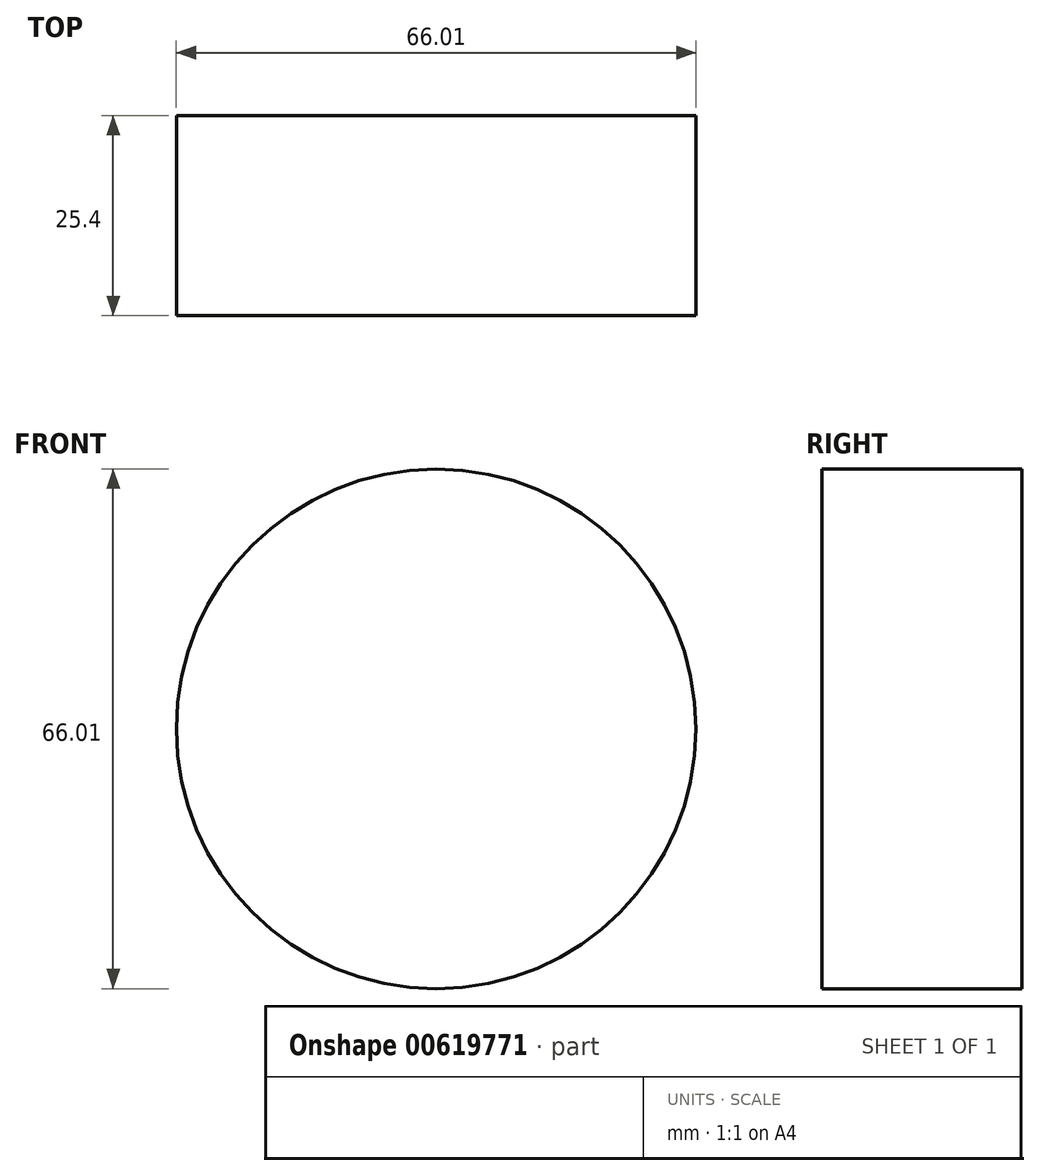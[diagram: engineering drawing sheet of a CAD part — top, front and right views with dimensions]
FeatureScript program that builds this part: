
annotation { "Feature Type Name" : "Feature", "Feature Type Description" : "" }
export const myFeature = defineFeature(function(context is Context, id is Id, definition is map)
    precondition{}
    {
        {
            var Q0;
            Q0=qCreatedBy(makeId("Front.planeOp"),FACE);
            var sketch = newSketch(context, id + "F0", { "sketchPlane" : qUnion([Q0])});
            skCircle(sketch, "E0", {"center": v(-43.02, 19.3) * mm, "radius": 33 * mm});
            skSolve(sketch);
        }
        {
            var Q0;
            Q0=makeQuery(id+"F0.imprint","IMPRINT",FACE,{"disambiguationData":[TD([[makeQuery(id+"F0.imprint","IMPRINT",EDGE,{"derivedFrom":sQuery(id+"F0.wireOp",EDGE,"E0")}),1.0]])]});
            extrude(context, id + "F1", {"entities" : qUnion([Q0]), "depth" : 25.4 * mm, "offsetDistance" : 25.4 * mm});
        }
    });
